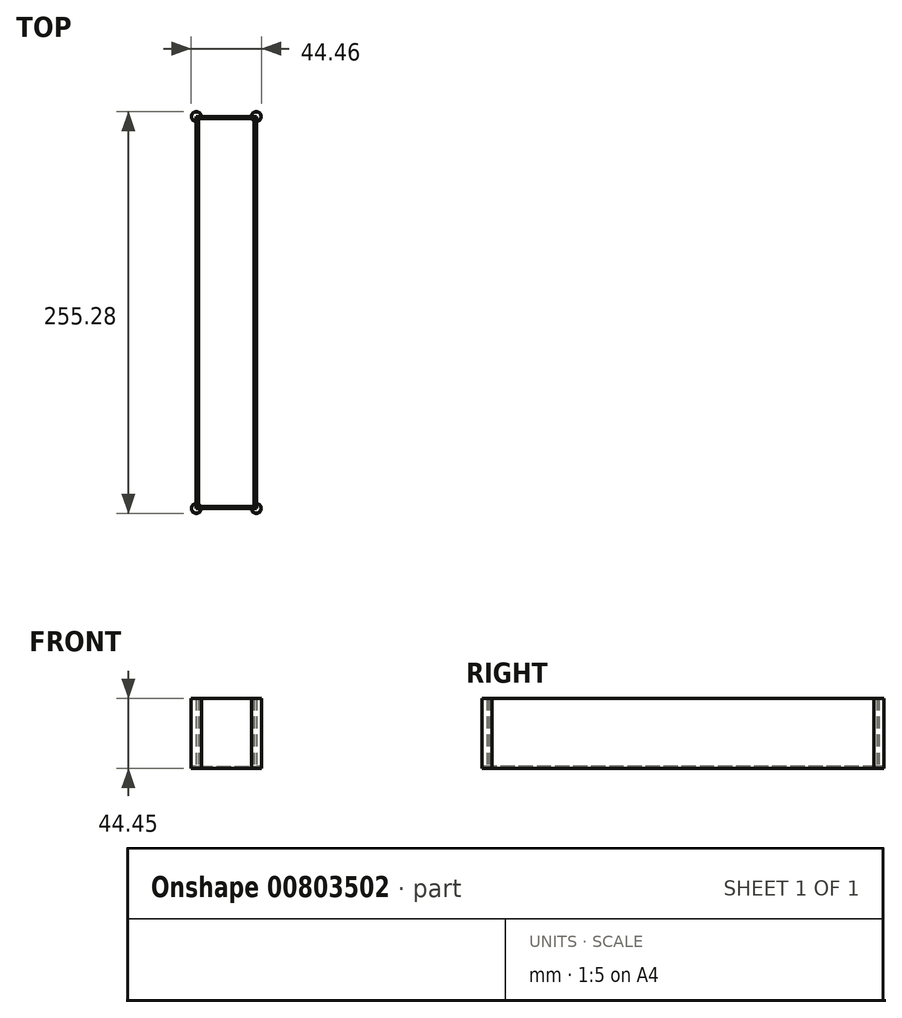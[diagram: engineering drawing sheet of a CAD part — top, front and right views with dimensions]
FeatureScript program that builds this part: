
annotation { "Feature Type Name" : "Feature", "Feature Type Description" : "" }
export const myFeature = defineFeature(function(context is Context, id is Id, definition is map)
    precondition{}
    {
        {
            var Q0;
            Q0=qCreatedBy(makeId("Top.planeOp"),FACE);
            var sketch = newSketch(context, id + "F0", { "sketchPlane" : qUnion([Q0])});
            skLineSegment(sketch, "E0.bottom", {"start": v(-19.05, 124.46) * mm, "end": v(19.05, 124.46) * mm});
            skLineSegment(sketch, "E0.top", {"start": v(-19.05, -124.46) * mm, "end": v(19.05, -124.46) * mm});
            skLineSegment(sketch, "E0.left", {"start": v(-19.05, 124.46) * mm, "end": v(-19.05, -124.46) * mm});
            skLineSegment(sketch, "E0.right", {"start": v(19.05, 124.46) * mm, "end": v(19.05, -124.46) * mm});
            skCircle(sketch, "E1", {"center": v(-19.05, 124.46) * mm, "radius": 3.18 * mm});
            skCircle(sketch, "E2", {"center": v(-19.05, 124.46) * mm, "radius": 2.92 * mm});
            skLineSegment(sketch, "E3", {"start": v(0, 124.46) * mm, "end": v(0, -124.46) * mm, "construction": true});
            skLineSegment(sketch, "E4", {"start": v(-19.05, 0) * mm, "end": v(19.05, 0) * mm, "construction": true});
            skCircle(sketch, "E5.MirrorC", {"center": v(19.05, 124.46) * mm, "radius": 3.18 * mm});
            skCircle(sketch, "E6.MirrorC", {"center": v(19.05, 124.46) * mm, "radius": 2.92 * mm});
            skCircle(sketch, "E7.MirrorC", {"center": v(-19.05, -124.46) * mm, "radius": 3.18 * mm});
            skCircle(sketch, "E8.MirrorC", {"center": v(-19.05, -124.46) * mm, "radius": 2.92 * mm});
            skCircle(sketch, "E9.MirrorC", {"center": v(19.05, -124.46) * mm, "radius": 3.18 * mm});
            skCircle(sketch, "E10.MirrorC", {"center": v(19.05, -124.46) * mm, "radius": 2.92 * mm});
            skLineSegment(sketch, "E11.bottom", {"start": v(-17.78, 123.2) * mm, "end": v(17.78, 123.2) * mm});
            skLineSegment(sketch, "E11.top", {"start": v(-17.78, -123.2) * mm, "end": v(17.78, -123.2) * mm});
            skLineSegment(sketch, "E11.left", {"start": v(-17.78, 123.2) * mm, "end": v(-17.78, -123.2) * mm});
            skLineSegment(sketch, "E11.right", {"start": v(17.78, 123.2) * mm, "end": v(17.78, -123.2) * mm});
            skSolve(sketch);
        }
        {
            var Q0;
            Q0=makeQuery(id+"F0.imprint","IMPRINT",FACE,{"disambiguationData":[TD([[makeQuery(id+"F0.imprint","IMPRINT",EDGE,{"derivedFrom":sQuery(id+"F0.wireOp",EDGE,"E0.bottom")}),-1.0]])]});
            var Q1;
            {var subQ5=sQuery(id+"F0.wireOp",EDGE,"E1");var subQ13=sQuery(id+"F0.wireOp",EDGE,"E0.bottom");var subQ14=makeQuery(id+"F0.imprint","INTERSECT",VERTEX,{"derivedFrom":[subQ13,subQ5]});Q1=makeQuery(id+"F0.imprint","IMPRINT",FACE,{"disambiguationData":[TD([[makeQuery(id+"F0.imprint","IMPRINT",EDGE,{"disambiguationData":[TD([[subQ14,-1.0]])],"derivedFrom":subQ13}),-1.0]])]});}
            var Q2;
            {var subQ0=sQuery(id+"F0.wireOp",EDGE,"E5.MirrorC");var subQ1=sQuery(id+"F0.wireOp",EDGE,"E0.bottom");var subQ2=makeQuery(id+"F0.imprint","INTERSECT",VERTEX,{"derivedFrom":[subQ1,subQ0]});Q2=makeQuery(id+"F0.imprint","IMPRINT",FACE,{"disambiguationData":[TD([[makeQuery(id+"F0.imprint","IMPRINT",EDGE,{"disambiguationData":[TD([[subQ2,-1.0]])],"derivedFrom":subQ1}),1.0]])]});}
            var Q3;
            {var subQ0=sQuery(id+"F0.wireOp",EDGE,"E1");var subQ1=sQuery(id+"F0.wireOp",EDGE,"E0.bottom");var subQ2=makeQuery(id+"F0.imprint","INTERSECT",VERTEX,{"derivedFrom":[subQ1,subQ0]});Q3=makeQuery(id+"F0.imprint","IMPRINT",FACE,{"disambiguationData":[TD([[makeQuery(id+"F0.imprint","IMPRINT",EDGE,{"disambiguationData":[TD([[subQ2,1.0]])],"derivedFrom":subQ1}),1.0]])]});}
            var Q4;
            {var subQ0=sQuery(id+"F0.wireOp",EDGE,"E0.left");var subQ1=sQuery(id+"F0.wireOp",EDGE,"E0.top");var subQ2=makeQuery(id+"F0.imprint","INTERSECT",VERTEX,{"derivedFrom":[subQ1,subQ0]});Q4=makeQuery(id+"F0.imprint","IMPRINT",FACE,{"disambiguationData":[TD([[makeQuery(id+"F0.imprint","IMPRINT",EDGE,{"disambiguationData":[TD([[subQ2,-1.0]])],"derivedFrom":subQ1}),1.0]])]});}
            var Q5;
            {var subQ0=sQuery(id+"F0.wireOp",EDGE,"E7.MirrorC");var subQ1=sQuery(id+"F0.wireOp",EDGE,"E0.top");var subQ2=makeQuery(id+"F0.imprint","INTERSECT",VERTEX,{"derivedFrom":[subQ1,subQ0]});Q5=makeQuery(id+"F0.imprint","IMPRINT",FACE,{"disambiguationData":[TD([[makeQuery(id+"F0.imprint","IMPRINT",EDGE,{"disambiguationData":[TD([[subQ2,1.0]])],"derivedFrom":subQ1}),-1.0]])]});}
            var Q6;
            {var subQ0=sQuery(id+"F0.wireOp",EDGE,"E0.right");var subQ1=sQuery(id+"F0.wireOp",EDGE,"E0.top");var subQ2=makeQuery(id+"F0.imprint","INTERSECT",VERTEX,{"derivedFrom":[subQ1,subQ0]});Q6=makeQuery(id+"F0.imprint","IMPRINT",FACE,{"disambiguationData":[TD([[makeQuery(id+"F0.imprint","IMPRINT",EDGE,{"disambiguationData":[TD([[subQ2,1.0]])],"derivedFrom":subQ1}),1.0]])]});}
            var Q7;
            {var subQ0=sQuery(id+"F0.wireOp",EDGE,"E9.MirrorC");var subQ1=sQuery(id+"F0.wireOp",EDGE,"E0.top");var subQ2=makeQuery(id+"F0.imprint","INTERSECT",VERTEX,{"derivedFrom":[subQ1,subQ0]});Q7=makeQuery(id+"F0.imprint","IMPRINT",FACE,{"disambiguationData":[TD([[makeQuery(id+"F0.imprint","IMPRINT",EDGE,{"disambiguationData":[TD([[subQ2,-1.0]])],"derivedFrom":subQ1}),-1.0]])]});}
            var Q8;
            {var subQ0=sQuery(id+"F0.wireOp",EDGE,"E9.MirrorC");var subQ1=sQuery(id+"F0.wireOp",EDGE,"E0.top");var subQ2=makeQuery(id+"F0.imprint","INTERSECT",VERTEX,{"derivedFrom":[subQ1,subQ0]});Q8=makeQuery(id+"F0.imprint","IMPRINT",FACE,{"disambiguationData":[TD([[makeQuery(id+"F0.imprint","IMPRINT",EDGE,{"disambiguationData":[TD([[subQ2,-1.0]])],"derivedFrom":subQ1}),1.0]])]});}
            var Q9;
            {var subQ0=sQuery(id+"F0.wireOp",EDGE,"E1");var subQ1=sQuery(id+"F0.wireOp",EDGE,"E0.left");var subQ2=makeQuery(id+"F0.imprint","INTERSECT",VERTEX,{"derivedFrom":[subQ1,subQ0]});Q9=makeQuery(id+"F0.imprint","IMPRINT",FACE,{"disambiguationData":[TD([[makeQuery(id+"F0.imprint","IMPRINT",EDGE,{"disambiguationData":[TD([[subQ2,-1.0]])],"derivedFrom":subQ1}),1.0]])]});}
            var Q10;
            {var subQ1=sQuery(id+"F0.wireOp",EDGE,"E0.bottom");var subQ5=sQuery(id+"F0.wireOp",EDGE,"E0.left");var subQ9=makeQuery(id+"F0.imprint","INTERSECT",VERTEX,{"derivedFrom":[subQ1,subQ5]});Q10=makeQuery(id+"F0.imprint","IMPRINT",FACE,{"disambiguationData":[TD([[makeQuery(id+"F0.imprint","IMPRINT",EDGE,{"disambiguationData":[TD([[subQ9,-1.0]])],"derivedFrom":subQ1}),-1.0]])]});}
            var Q11;
            {var subQ0=sQuery(id+"F0.wireOp",EDGE,"E5.MirrorC");var subQ1=sQuery(id+"F0.wireOp",EDGE,"E0.right");var subQ2=makeQuery(id+"F0.imprint","INTERSECT",VERTEX,{"derivedFrom":[subQ1,subQ0]});Q11=makeQuery(id+"F0.imprint","IMPRINT",FACE,{"disambiguationData":[TD([[makeQuery(id+"F0.imprint","IMPRINT",EDGE,{"disambiguationData":[TD([[subQ2,-1.0]])],"derivedFrom":subQ1}),-1.0]])]});}
            var Q12;
            {var subQ1=sQuery(id+"F0.wireOp",EDGE,"E0.right");var subQ5=sQuery(id+"F0.wireOp",EDGE,"E0.bottom");var subQ9=makeQuery(id+"F0.imprint","INTERSECT",VERTEX,{"derivedFrom":[subQ5,subQ1]});Q12=makeQuery(id+"F0.imprint","IMPRINT",FACE,{"disambiguationData":[TD([[makeQuery(id+"F0.imprint","IMPRINT",EDGE,{"disambiguationData":[TD([[subQ9,1.0]])],"derivedFrom":subQ5}),-1.0]])]});}
            var Q13;
            {var subQ0=sQuery(id+"F0.wireOp",EDGE,"E7.MirrorC");var subQ1=sQuery(id+"F0.wireOp",EDGE,"E0.top");var subQ2=makeQuery(id+"F0.imprint","INTERSECT",VERTEX,{"derivedFrom":[subQ1,subQ0]});Q13=makeQuery(id+"F0.imprint","IMPRINT",FACE,{"disambiguationData":[TD([[makeQuery(id+"F0.imprint","IMPRINT",EDGE,{"disambiguationData":[TD([[subQ2,-1.0]])],"derivedFrom":subQ1}),1.0]])]});}
            var Q14;
            {var subQ0=sQuery(id+"F0.wireOp",EDGE,"E9.MirrorC");var subQ1=sQuery(id+"F0.wireOp",EDGE,"E0.right");var subQ2=makeQuery(id+"F0.imprint","INTERSECT",VERTEX,{"derivedFrom":[subQ1,subQ0]});Q14=makeQuery(id+"F0.imprint","IMPRINT",FACE,{"disambiguationData":[TD([[makeQuery(id+"F0.imprint","IMPRINT",EDGE,{"disambiguationData":[TD([[subQ2,-1.0]])],"derivedFrom":subQ1}),-1.0]])]});}
            var Q15;
            {var subQ0=sQuery(id+"F0.wireOp",EDGE,"E7.MirrorC");var subQ1=sQuery(id+"F0.wireOp",EDGE,"E0.top");var subQ2=makeQuery(id+"F0.imprint","INTERSECT",VERTEX,{"derivedFrom":[subQ1,subQ0]});Q15=makeQuery(id+"F0.imprint","IMPRINT",FACE,{"disambiguationData":[TD([[makeQuery(id+"F0.imprint","IMPRINT",EDGE,{"disambiguationData":[TD([[subQ2,1.0]])],"derivedFrom":subQ1}),1.0]])]});}
            var Q16;
            {var subQ0=sQuery(id+"F0.wireOp",EDGE,"E7.MirrorC");var subQ1=sQuery(id+"F0.wireOp",EDGE,"E0.left");var subQ2=makeQuery(id+"F0.imprint","INTERSECT",VERTEX,{"derivedFrom":[subQ1,subQ0]});Q16=makeQuery(id+"F0.imprint","IMPRINT",FACE,{"disambiguationData":[TD([[makeQuery(id+"F0.imprint","IMPRINT",EDGE,{"disambiguationData":[TD([[subQ2,-1.0]])],"derivedFrom":subQ1}),1.0]])]});}
            var Q17;
            {var subQ0=sQuery(id+"F0.wireOp",EDGE,"E5.MirrorC");var subQ1=sQuery(id+"F0.wireOp",EDGE,"E0.right");var subQ2=makeQuery(id+"F0.imprint","INTERSECT",VERTEX,{"derivedFrom":[subQ1,subQ0]});Q17=makeQuery(id+"F0.imprint","IMPRINT",FACE,{"disambiguationData":[TD([[makeQuery(id+"F0.imprint","IMPRINT",EDGE,{"disambiguationData":[TD([[subQ2,1.0]])],"derivedFrom":subQ1}),-1.0]])]});}
            var Q18;
            {var subQ0=sQuery(id+"F0.wireOp",EDGE,"E1");var subQ1=sQuery(id+"F0.wireOp",EDGE,"E0.left");var subQ2=makeQuery(id+"F0.imprint","INTERSECT",VERTEX,{"derivedFrom":[subQ1,subQ0]});Q18=makeQuery(id+"F0.imprint","IMPRINT",FACE,{"disambiguationData":[TD([[makeQuery(id+"F0.imprint","IMPRINT",EDGE,{"disambiguationData":[TD([[subQ2,1.0]])],"derivedFrom":subQ1}),1.0]])]});}
            extrude(context, id + "F1", {"entities" : qUnion([Q0, Q1, Q2, Q3, Q4, Q5, Q6, Q7, Q8, Q9, Q10, Q11, Q12, Q13, Q14, Q15, Q16, Q17, Q18]), "depth" : 44.45 * mm, "offsetDistance" : 25.4 * mm});
        }
        {
            var Q0;
            {var subQ5=sQuery(id+"F0.wireOp",EDGE,"E11.left");var subQ13=sQuery(id+"F0.wireOp",EDGE,"E1");var subQ14=makeQuery(id+"F0.imprint","INTERSECT",VERTEX,{"derivedFrom":[subQ13,subQ5]});Q0=makeQuery(id+"F0.imprint","IMPRINT",FACE,{"disambiguationData":[TD([[makeQuery(id+"F0.imprint","IMPRINT",EDGE,{"disambiguationData":[TD([[subQ14,-1.0]])],"derivedFrom":subQ13}),-1.0]])]});}
            var Q1;
            {var subQ0=sQuery(id+"F0.wireOp",EDGE,"E11.left");var subQ1=sQuery(id+"F0.wireOp",EDGE,"E2");var subQ2=makeQuery(id+"F0.imprint","INTERSECT",VERTEX,{"derivedFrom":[subQ1,subQ0]});Q1=makeQuery(id+"F0.imprint","IMPRINT",FACE,{"disambiguationData":[TD([[makeQuery(id+"F0.imprint","IMPRINT",EDGE,{"disambiguationData":[TD([[subQ2,-1.0]])],"derivedFrom":subQ1}),1.0]])]});}
            var Q2;
            {var subQ0=sQuery(id+"F0.wireOp",EDGE,"E11.left");var subQ1=sQuery(id+"F0.wireOp",EDGE,"E1");var subQ2=makeQuery(id+"F0.imprint","INTERSECT",VERTEX,{"derivedFrom":[subQ1,subQ0]});Q2=makeQuery(id+"F0.imprint","IMPRINT",FACE,{"disambiguationData":[TD([[makeQuery(id+"F0.imprint","IMPRINT",EDGE,{"disambiguationData":[TD([[subQ2,-1.0]])],"derivedFrom":subQ1}),1.0]])]});}
            var Q3;
            {var subQ0=sQuery(id+"F0.wireOp",EDGE,"E11.right");var subQ1=sQuery(id+"F0.wireOp",EDGE,"E6.MirrorC");var subQ2=makeQuery(id+"F0.imprint","INTERSECT",VERTEX,{"derivedFrom":[subQ1,subQ0]});Q3=makeQuery(id+"F0.imprint","IMPRINT",FACE,{"disambiguationData":[TD([[makeQuery(id+"F0.imprint","IMPRINT",EDGE,{"disambiguationData":[TD([[subQ2,-1.0]])],"derivedFrom":subQ1}),-1.0]])]});}
            var Q4;
            {var subQ0=sQuery(id+"F0.wireOp",EDGE,"E11.right");var subQ1=sQuery(id+"F0.wireOp",EDGE,"E5.MirrorC");var subQ2=makeQuery(id+"F0.imprint","INTERSECT",VERTEX,{"derivedFrom":[subQ1,subQ0]});Q4=makeQuery(id+"F0.imprint","IMPRINT",FACE,{"disambiguationData":[TD([[makeQuery(id+"F0.imprint","IMPRINT",EDGE,{"disambiguationData":[TD([[subQ2,-1.0]])],"derivedFrom":subQ1}),-1.0]])]});}
            var Q5;
            {var subQ0=sQuery(id+"F0.wireOp",EDGE,"E11.right");var subQ1=sQuery(id+"F0.wireOp",EDGE,"E10.MirrorC");var subQ2=makeQuery(id+"F0.imprint","INTERSECT",VERTEX,{"derivedFrom":[subQ1,subQ0]});Q5=makeQuery(id+"F0.imprint","IMPRINT",FACE,{"disambiguationData":[TD([[makeQuery(id+"F0.imprint","IMPRINT",EDGE,{"disambiguationData":[TD([[subQ2,-1.0]])],"derivedFrom":subQ1}),1.0]])]});}
            var Q6;
            {var subQ0=sQuery(id+"F0.wireOp",EDGE,"E11.right");var subQ1=sQuery(id+"F0.wireOp",EDGE,"E9.MirrorC");var subQ2=makeQuery(id+"F0.imprint","INTERSECT",VERTEX,{"derivedFrom":[subQ1,subQ0]});Q6=makeQuery(id+"F0.imprint","IMPRINT",FACE,{"disambiguationData":[TD([[makeQuery(id+"F0.imprint","IMPRINT",EDGE,{"disambiguationData":[TD([[subQ2,-1.0]])],"derivedFrom":subQ1}),1.0]])]});}
            var Q7;
            {var subQ0=sQuery(id+"F0.wireOp",EDGE,"E11.left");var subQ1=sQuery(id+"F0.wireOp",EDGE,"E7.MirrorC");var subQ2=makeQuery(id+"F0.imprint","INTERSECT",VERTEX,{"derivedFrom":[subQ1,subQ0]});Q7=makeQuery(id+"F0.imprint","IMPRINT",FACE,{"disambiguationData":[TD([[makeQuery(id+"F0.imprint","IMPRINT",EDGE,{"disambiguationData":[TD([[subQ2,-1.0]])],"derivedFrom":subQ1}),-1.0]])]});}
            var Q8;
            {var subQ0=sQuery(id+"F0.wireOp",EDGE,"E11.left");var subQ1=sQuery(id+"F0.wireOp",EDGE,"E8.MirrorC");var subQ2=makeQuery(id+"F0.imprint","INTERSECT",VERTEX,{"derivedFrom":[subQ1,subQ0]});Q8=makeQuery(id+"F0.imprint","IMPRINT",FACE,{"disambiguationData":[TD([[makeQuery(id+"F0.imprint","IMPRINT",EDGE,{"disambiguationData":[TD([[subQ2,-1.0]])],"derivedFrom":subQ1}),-1.0]])]});}
            var Q9;
            {var subQ0=sQuery(id+"F0.wireOp",EDGE,"E0.right");var subQ1=sQuery(id+"F0.wireOp",EDGE,"E0.top");var subQ2=makeQuery(id+"F0.imprint","INTERSECT",VERTEX,{"derivedFrom":[subQ1,subQ0]});Q9=makeQuery(id+"F0.imprint","IMPRINT",FACE,{"disambiguationData":[TD([[makeQuery(id+"F0.imprint","IMPRINT",EDGE,{"disambiguationData":[TD([[subQ2,1.0]])],"derivedFrom":subQ1}),-1.0]])]});}
            var Q10;
            {var subQ0=sQuery(id+"F0.wireOp",EDGE,"E0.left");var subQ1=sQuery(id+"F0.wireOp",EDGE,"E0.top");var subQ2=makeQuery(id+"F0.imprint","INTERSECT",VERTEX,{"derivedFrom":[subQ1,subQ0]});Q10=makeQuery(id+"F0.imprint","IMPRINT",FACE,{"disambiguationData":[TD([[makeQuery(id+"F0.imprint","IMPRINT",EDGE,{"disambiguationData":[TD([[subQ2,-1.0]])],"derivedFrom":subQ1}),-1.0]])]});}
            var Q11;
            {var subQ0=sQuery(id+"F0.wireOp",EDGE,"E0.right");var subQ1=sQuery(id+"F0.wireOp",EDGE,"E0.bottom");var subQ2=makeQuery(id+"F0.imprint","INTERSECT",VERTEX,{"derivedFrom":[subQ1,subQ0]});Q11=makeQuery(id+"F0.imprint","IMPRINT",FACE,{"disambiguationData":[TD([[makeQuery(id+"F0.imprint","IMPRINT",EDGE,{"disambiguationData":[TD([[subQ2,1.0]])],"derivedFrom":subQ1}),1.0]])]});}
            var Q12;
            {var subQ0=sQuery(id+"F0.wireOp",EDGE,"E0.left");var subQ1=sQuery(id+"F0.wireOp",EDGE,"E0.bottom");var subQ2=makeQuery(id+"F0.imprint","INTERSECT",VERTEX,{"derivedFrom":[subQ1,subQ0]});Q12=makeQuery(id+"F0.imprint","IMPRINT",FACE,{"disambiguationData":[TD([[makeQuery(id+"F0.imprint","IMPRINT",EDGE,{"disambiguationData":[TD([[subQ2,-1.0]])],"derivedFrom":subQ1}),1.0]])]});}
            extrude(context, id + "F2", {"entities" : qUnion([Q0, Q1, Q2, Q3, Q4, Q5, Q6, Q7, Q8, Q9, Q10, Q11, Q12]), "operationType" : NewBodyOperationType.ADD, "depth" : 1.27 * mm, "offsetDistance" : 25.4 * mm});
        }
    });
